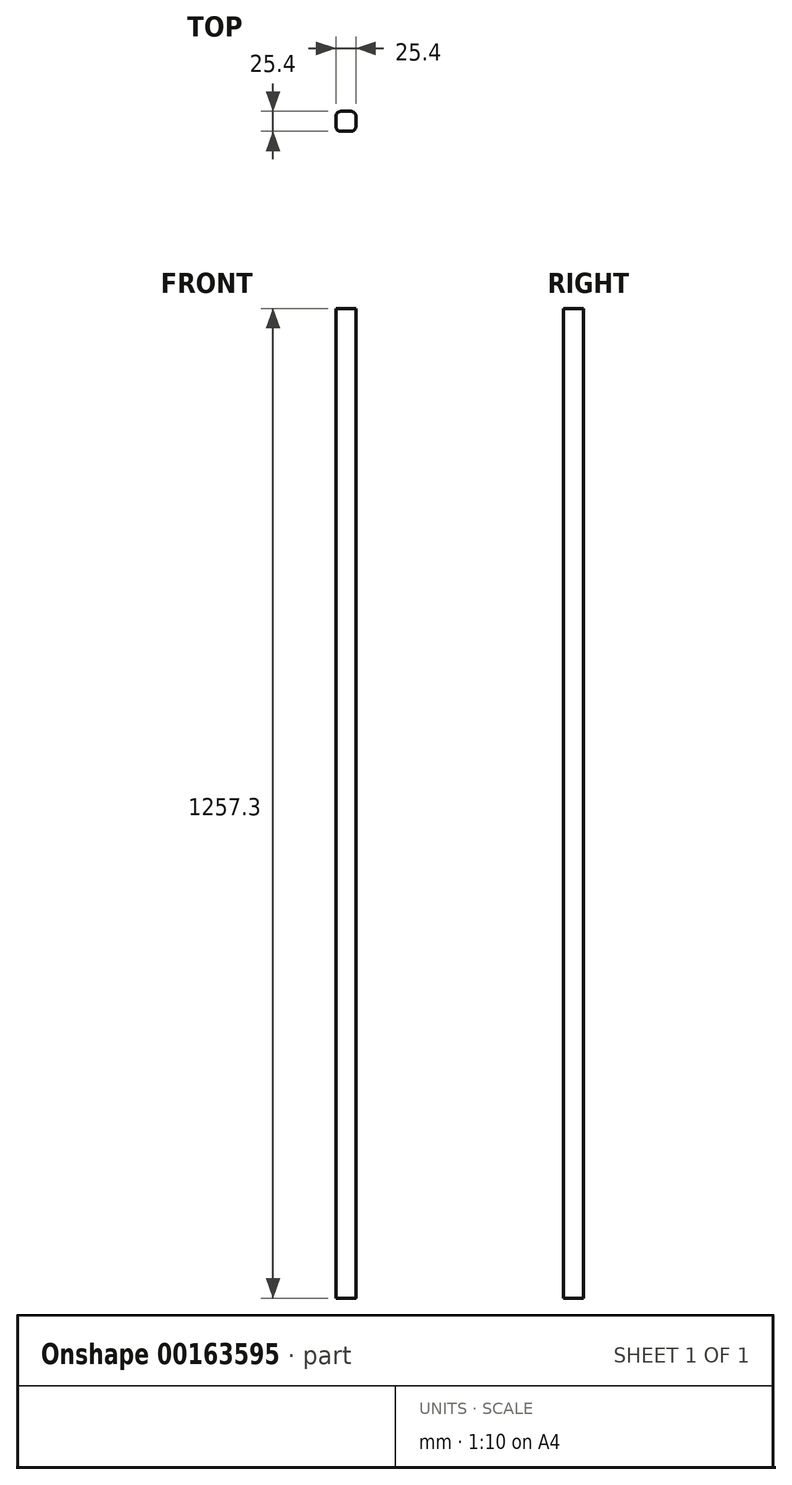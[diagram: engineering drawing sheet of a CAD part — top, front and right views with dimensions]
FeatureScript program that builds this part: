
annotation { "Feature Type Name" : "Feature", "Feature Type Description" : "" }
export const myFeature = defineFeature(function(context is Context, id is Id, definition is map)
    precondition{}
    {
        {
            var Q0;
            Q0=qCreatedBy(makeId("Top.planeOp"),FACE);
            var sketch = newSketch(context, id + "F0", { "sketchPlane" : qUnion([Q0])});
            skLineSegment(sketch, "E0.bottom", {"start": v(6.35, 12.7) * mm, "end": v(-6.35, 12.7) * mm});
            skLineSegment(sketch, "E0.top", {"start": v(6.35, -12.7) * mm, "end": v(-6.35, -12.7) * mm});
            skLineSegment(sketch, "E0.left", {"start": v(12.7, 6.35) * mm, "end": v(12.7, -6.35) * mm});
            skLineSegment(sketch, "E0.right", {"start": v(-12.7, 6.35) * mm, "end": v(-12.7, -6.35) * mm});
            skPoint(sketch, "E0.middle", {"position": v(0, 0) * mm});
            skPoint(sketch, "E1.visualSharp", {"position": v(-12.7, 12.7) * mm});
            skArc(sketch, "E1.filletArc", {"start": v(-6.35, 12.7) * mm, "mid": v(-10.84, 10.84) * mm, "end": v(-12.7, 6.35) * mm});
            skPoint(sketch, "E2.visualSharp", {"position": v(12.7, 12.7) * mm});
            skArc(sketch, "E2.filletArc", {"start": v(12.7, 6.35) * mm, "mid": v(10.84, 10.84) * mm, "end": v(6.35, 12.7) * mm});
            skPoint(sketch, "E3.visualSharp", {"position": v(12.7, -12.7) * mm});
            skArc(sketch, "E3.filletArc", {"start": v(6.35, -12.7) * mm, "mid": v(10.84, -10.84) * mm, "end": v(12.7, -6.35) * mm});
            skPoint(sketch, "E4.visualSharp", {"position": v(-12.7, -12.7) * mm});
            skArc(sketch, "E4.filletArc", {"start": v(-12.7, -6.35) * mm, "mid": v(-10.84, -10.84) * mm, "end": v(-6.35, -12.7) * mm});
            skSolve(sketch);
        }
        {
            var Q0;
            Q0=makeQuery(id+"F0.imprint","IMPRINT",FACE,{"disambiguationData":[TD([[makeQuery(id+"F0.imprint","IMPRINT",EDGE,{"derivedFrom":sQuery(id+"F0.wireOp",EDGE,"E0.bottom")}),1.0]])]});
            extrude(context, id + "F1", {"entities" : qUnion([Q0]), "depth" : 1257.3 * mm});
        }
    });
